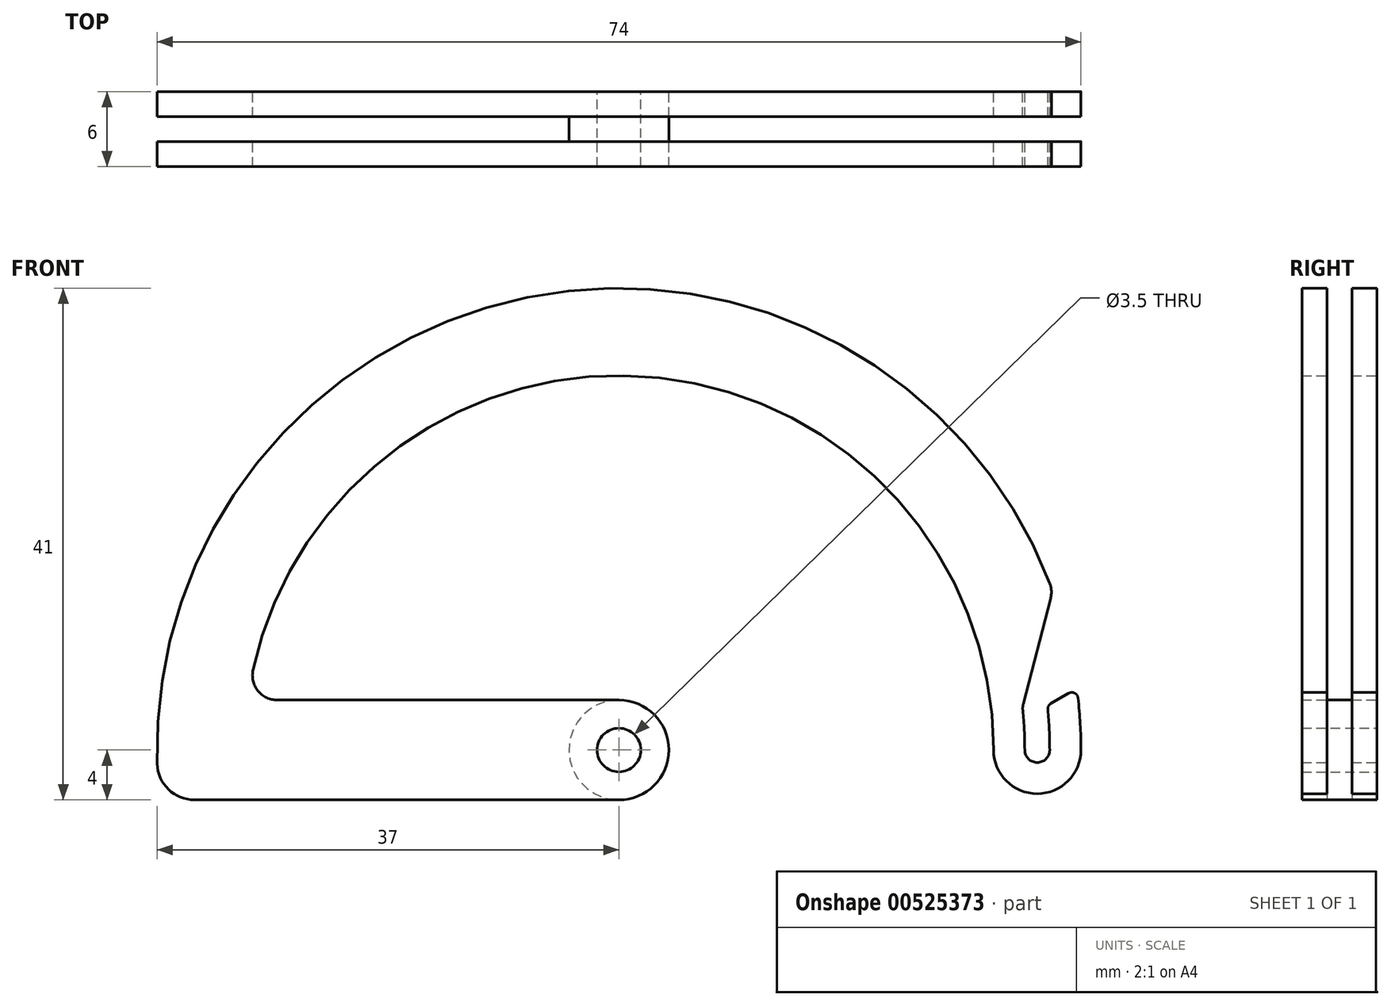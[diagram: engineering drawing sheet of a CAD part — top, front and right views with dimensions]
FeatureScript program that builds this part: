
annotation { "Feature Type Name" : "Feature", "Feature Type Description" : "" }
export const myFeature = defineFeature(function(context is Context, id is Id, definition is map)
    precondition{}
    {
        {
            var Q0;
            Q0=qCreatedBy(makeId("Front.planeOp"),FACE);
            var sketch = newSketch(context, id + "F0", { "sketchPlane" : qUnion([Q0])});
            skLineSegment(sketch, "E0", {"start": v(34.6, 3.72) * mm, "end": v(36.02, 4.55) * mm});
            skLineSegment(sketch, "E1", {"start": v(32.38, 3.7) * mm, "end": v(34.57, 12.16) * mm});
            skArc(sketch, "E2", {"start": v(32.5, 0) * mm, "mid": v(33.5, -1) * mm, "end": v(34.5, 0) * mm});
            skArc(sketch, "E3", {"start": v(32.5, 0) * mm, "mid": v(32.46, 1.59) * mm, "end": v(32.34, 3.17) * mm});
            skArc(sketch, "E4", {"start": v(34.5, 0) * mm, "mid": v(34.46, 1.62) * mm, "end": v(34.35, 3.24) * mm});
            skArc(sketch, "E5", {"start": v(30, 0) * mm, "mid": v(33.5, -3.5) * mm, "end": v(37, 0) * mm});
            skArc(sketch, "E6", {"start": v(34.5, 13.38) * mm, "mid": v(-7.34, 36.26) * mm, "end": v(-36.98, -1.09) * mm});
            skPoint(sketch, "E7.visualSharp", {"position": v(34.32, 3.56) * mm});
            skArc(sketch, "E7.filletArc", {"start": v(34.6, 3.72) * mm, "mid": v(34.4, 3.52) * mm, "end": v(34.35, 3.24) * mm});
            skPoint(sketch, "E8.visualSharp", {"position": v(36.67, 4.93) * mm});
            skArc(sketch, "E8.filletArc", {"start": v(36.76, 4.17) * mm, "mid": v(36.5, 4.56) * mm, "end": v(36.02, 4.55) * mm});
            skPoint(sketch, "E9.visualSharp", {"position": v(32.32, 3.44) * mm});
            skArc(sketch, "E9.filletArc", {"start": v(32.38, 3.7) * mm, "mid": v(32.34, 3.44) * mm, "end": v(32.34, 3.17) * mm});
            skPoint(sketch, "E10.visualSharp", {"position": v(34.73, 12.77) * mm});
            skArc(sketch, "E10.filletArc", {"start": v(34.57, 12.16) * mm, "mid": v(34.63, 12.77) * mm, "end": v(34.5, 13.38) * mm});
            skArc(sketch, "E11", {"start": v(30, 0) * mm, "mid": v(3.23, 29.83) * mm, "end": v(-29.3, 6.43) * mm});
            skArc(sketch, "E12", {"start": v(37, 0) * mm, "mid": v(36.94, 2.1) * mm, "end": v(36.76, 4.17) * mm});
            skLineSegment(sketch, "E13", {"start": v(0, 4) * mm, "end": v(-27.35, 4) * mm});
            skLineSegment(sketch, "E14", {"start": v(0, -4) * mm, "end": v(-29.73, -4) * mm});
            skLineSegment(sketch, "E15", {"start": v(-29.73, -4) * mm, "end": v(-33.99, -4) * mm});
            skArc(sketch, "E16", {"start": v(0, -4) * mm, "mid": v(4, 0) * mm, "end": v(0, 4) * mm});
            skPoint(sketch, "E17.visualSharp", {"position": v(-29.73, 4) * mm});
            skArc(sketch, "E17.filletArc", {"start": v(-29.3, 6.43) * mm, "mid": v(-28.9, 4.75) * mm, "end": v(-27.35, 4) * mm});
            skPoint(sketch, "E18.visualSharp", {"position": v(-36.78, -4) * mm});
            skArc(sketch, "E18.filletArc", {"start": v(-36.98, -1.09) * mm, "mid": v(-36.08, -3.15) * mm, "end": v(-33.99, -4) * mm});
            skSolve(sketch);
        }
        {
            var Q0;
            Q0=makeQuery(id+"F0.imprint","IMPRINT",FACE,{"disambiguationData":[TD([[makeQuery(id+"F0.imprint","IMPRINT",EDGE,{"derivedFrom":sQuery(id+"F0.wireOp",EDGE,"E0")}),-1.0]])]});
            extrude(context, id + "F1", {"entities" : qUnion([Q0]), "depth" : 2 * mm, "offsetDistance" : 25.4 * mm});
        }
        {
            var Q0;
            Q0=makeQuery(id+"F1.opExtrude","CAP_FACE",FACE,{"disambiguationData":[OSD([sQuery(id+"F0.wireOp",EDGE,"E0"),sQuery(id+"F0.wireOp",EDGE,"E1"),sQuery(id+"F0.wireOp",EDGE,"E2"),sQuery(id+"F0.wireOp",EDGE,"E3"),sQuery(id+"F0.wireOp",EDGE,"E4"),sQuery(id+"F0.wireOp",EDGE,"E5"),sQuery(id+"F0.wireOp",EDGE,"E6"),sQuery(id+"F0.wireOp",EDGE,"E7.filletArc"),sQuery(id+"F0.wireOp",EDGE,"E8.filletArc"),sQuery(id+"F0.wireOp",EDGE,"E9.filletArc"),sQuery(id+"F0.wireOp",EDGE,"E10.filletArc"),sQuery(id+"F0.wireOp",EDGE,"E11"),sQuery(id+"F0.wireOp",EDGE,"E12"),sQuery(id+"F0.wireOp",EDGE,"E13"),sQuery(id+"F0.wireOp",EDGE,"E14"),sQuery(id+"F0.wireOp",EDGE,"E15"),sQuery(id+"F0.wireOp",EDGE,"E16"),sQuery(id+"F0.wireOp",EDGE,"E17.filletArc"),sQuery(id+"F0.wireOp",EDGE,"E18.filletArc")])],"isStart":false});
            var sketch = newSketch(context, id + "F2", { "sketchPlane" : qUnion([Q0])});
            skCircle(sketch, "E19", {"center": v(0, 0) * mm, "radius": 4 * mm});
            skSolve(sketch);
        }
        {
            var Q0;
            {var subQ0=sQuery(id+"F2.wireOp",EDGE,"E19");var subQ1=makeQuery(id+"F2.imprint","INTERSECT",VERTEX,{"derivedFrom":[makeQuery(id+"F1.opExtrude","CAP_EDGE",EDGE,{"disambiguationData":[OSD([sQuery(id+"F0.wireOp",EDGE,"E13")])],"isStart":false}),subQ0]});Q0=makeQuery(id+"F2.imprint","IMPRINT",FACE,{"disambiguationData":[TD([[makeQuery(id+"F2.imprint","IMPRINT",EDGE,{"disambiguationData":[TD([[subQ1,1.0]])],"derivedFrom":subQ0}),1.0]])]});}
            extrude(context, id + "F3", {"entities" : qUnion([Q0]), "operationType" : NewBodyOperationType.ADD, "depth" : 2 * mm, "offsetDistance" : 25.4 * mm});
        }
        {
            var Q0;
            Q0=makeQuery(id+"F3.opExtrude","CAP_FACE",FACE,{"disambiguationData":[OSD([sQuery(id+"F2.wireOp",EDGE,"E19")])],"isStart":false});
            var sketch = newSketch(context, id + "F4", { "sketchPlane" : qUnion([Q0])});
            skLineSegment(sketch, "E20", {"start": v(34.6, 3.72) * mm, "end": v(36.02, 4.55) * mm});
            skLineSegment(sketch, "E21", {"start": v(32.38, 3.7) * mm, "end": v(34.57, 12.16) * mm});
            skArc(sketch, "E22", {"start": v(32.5, 0) * mm, "mid": v(33.5, -1) * mm, "end": v(34.5, 0) * mm});
            skArc(sketch, "E23", {"start": v(32.5, 0) * mm, "mid": v(32.46, 1.59) * mm, "end": v(32.34, 3.17) * mm});
            skArc(sketch, "E24", {"start": v(34.5, 0) * mm, "mid": v(34.46, 1.62) * mm, "end": v(34.35, 3.24) * mm});
            skArc(sketch, "E25", {"start": v(30, 0) * mm, "mid": v(33.5, -3.5) * mm, "end": v(37, 0) * mm});
            skArc(sketch, "E26", {"start": v(34.5, 13.38) * mm, "mid": v(-7.34, 36.26) * mm, "end": v(-36.98, -1.09) * mm});
            skPoint(sketch, "E27.visualSharp", {"position": v(34.32, 3.56) * mm});
            skArc(sketch, "E27.filletArc", {"start": v(34.6, 3.72) * mm, "mid": v(34.4, 3.52) * mm, "end": v(34.35, 3.24) * mm});
            skPoint(sketch, "E28.visualSharp", {"position": v(36.67, 4.93) * mm});
            skArc(sketch, "E28.filletArc", {"start": v(36.76, 4.17) * mm, "mid": v(36.5, 4.56) * mm, "end": v(36.02, 4.55) * mm});
            skPoint(sketch, "E29.visualSharp", {"position": v(32.32, 3.44) * mm});
            skArc(sketch, "E29.filletArc", {"start": v(32.38, 3.7) * mm, "mid": v(32.34, 3.44) * mm, "end": v(32.34, 3.17) * mm});
            skPoint(sketch, "E30.visualSharp", {"position": v(34.73, 12.77) * mm});
            skArc(sketch, "E30.filletArc", {"start": v(34.57, 12.16) * mm, "mid": v(34.63, 12.77) * mm, "end": v(34.5, 13.38) * mm});
            skArc(sketch, "E31", {"start": v(30, 0) * mm, "mid": v(3.23, 29.83) * mm, "end": v(-29.3, 6.43) * mm});
            skArc(sketch, "E32", {"start": v(37, 0) * mm, "mid": v(36.94, 2.1) * mm, "end": v(36.76, 4.17) * mm});
            skLineSegment(sketch, "E33", {"start": v(0, 4) * mm, "end": v(-27.35, 4) * mm});
            skLineSegment(sketch, "E34", {"start": v(0, -4) * mm, "end": v(-29.73, -4) * mm});
            skLineSegment(sketch, "E35", {"start": v(-29.73, -4) * mm, "end": v(-33.99, -4) * mm});
            skArc(sketch, "E36", {"start": v(0, -4) * mm, "mid": v(4, 0) * mm, "end": v(0, 4) * mm});
            skPoint(sketch, "E37.visualSharp", {"position": v(-29.73, 4) * mm});
            skArc(sketch, "E37.filletArc", {"start": v(-29.3, 6.43) * mm, "mid": v(-28.9, 4.75) * mm, "end": v(-27.35, 4) * mm});
            skPoint(sketch, "E38.visualSharp", {"position": v(-36.78, -4) * mm});
            skArc(sketch, "E38.filletArc", {"start": v(-36.98, -1.09) * mm, "mid": v(-36.08, -3.15) * mm, "end": v(-33.99, -4) * mm});
            skSolve(sketch);
        }
        {
            var Q0;
            Q0=makeQuery(id+"F4.imprint","IMPRINT",FACE,{"disambiguationData":[TD([[makeQuery(id+"F4.imprint","IMPRINT",EDGE,{"derivedFrom":sQuery(id+"F4.wireOp",EDGE,"E20")}),-1.0]])]});
            var Q1;
            {var subQ0=sQuery(id+"F4.wireOp",EDGE,"E36");Q1=makeQuery(id+"F4.imprint","IMPRINT",FACE,{"disambiguationData":[TD([[makeQuery(id+"F4.imprint","IMPRINT",EDGE,{"derivedFrom":subQ0}),1.0]])]});}
            extrude(context, id + "F5", {"entities" : qUnion([Q0, Q1]), "operationType" : NewBodyOperationType.ADD, "depth" : 2 * mm, "offsetDistance" : 25.4 * mm});
        }
        {
            var Q0;
            Q0=makeQuery(id+"F1.opExtrude","CAP_FACE",FACE,{"disambiguationData":[OSD([sQuery(id+"F0.wireOp",EDGE,"E0"),sQuery(id+"F0.wireOp",EDGE,"E1"),sQuery(id+"F0.wireOp",EDGE,"E2"),sQuery(id+"F0.wireOp",EDGE,"E3"),sQuery(id+"F0.wireOp",EDGE,"E4"),sQuery(id+"F0.wireOp",EDGE,"E5"),sQuery(id+"F0.wireOp",EDGE,"E6"),sQuery(id+"F0.wireOp",EDGE,"E7.filletArc"),sQuery(id+"F0.wireOp",EDGE,"E8.filletArc"),sQuery(id+"F0.wireOp",EDGE,"E9.filletArc"),sQuery(id+"F0.wireOp",EDGE,"E10.filletArc"),sQuery(id+"F0.wireOp",EDGE,"E11"),sQuery(id+"F0.wireOp",EDGE,"E12"),sQuery(id+"F0.wireOp",EDGE,"E13"),sQuery(id+"F0.wireOp",EDGE,"E14"),sQuery(id+"F0.wireOp",EDGE,"E15"),sQuery(id+"F0.wireOp",EDGE,"E16"),sQuery(id+"F0.wireOp",EDGE,"E17.filletArc"),sQuery(id+"F0.wireOp",EDGE,"E18.filletArc")])],"isStart":true});
            var sketch = newSketch(context, id + "F6", { "sketchPlane" : qUnion([Q0])});
            skCircle(sketch, "E39", {"center": v(0, 0) * mm, "radius": 1.75 * mm});
            skSolve(sketch);
        }
        {
            var Q0;
            Q0 = qSketchRegion(id + "F6", true);
            extrude(context, id + "F7", {"entities" : qUnion([Q0]), "operationType" : NewBodyOperationType.REMOVE, "oppositeDirection" : true, "depth" : 6 * mm, "offsetDistance" : 25.4 * mm});
        }
    });
